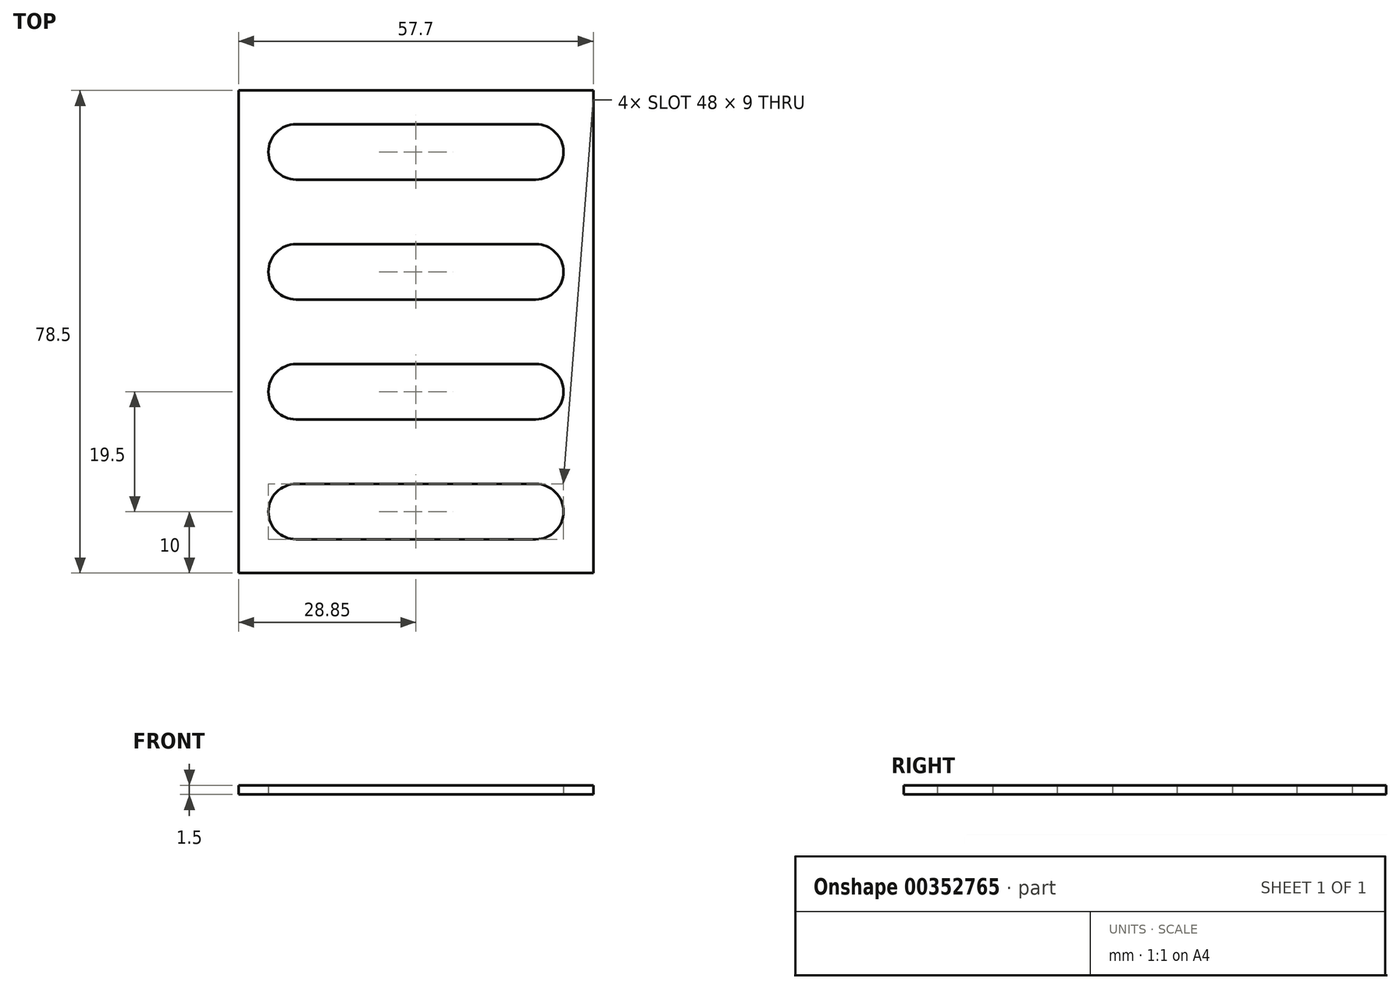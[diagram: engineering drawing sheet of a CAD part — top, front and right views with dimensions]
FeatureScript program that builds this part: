
annotation { "Feature Type Name" : "Feature", "Feature Type Description" : "" }
export const myFeature = defineFeature(function(context is Context, id is Id, definition is map)
    precondition{}
    {
        {
            var Q0;
            Q0=qCreatedBy(makeId("Top.planeOp"),FACE);
            var sketch = newSketch(context, id + "F0", { "sketchPlane" : qUnion([Q0])});
            skLineSegment(sketch, "E0.bottom", {"start": v(28.85, 39.25) * mm, "end": v(-28.85, 39.25) * mm});
            skLineSegment(sketch, "E0.top", {"start": v(28.85, -39.25) * mm, "end": v(-28.85, -39.25) * mm});
            skLineSegment(sketch, "E0.left", {"start": v(28.85, 39.25) * mm, "end": v(28.85, -39.25) * mm});
            skLineSegment(sketch, "E0.right", {"start": v(-28.85, 39.25) * mm, "end": v(-28.85, -39.25) * mm});
            skPoint(sketch, "E0.middle", {"position": v(0, 0) * mm});
            skLineSegment(sketch, "E1", {"start": v(-19.5, 29.25) * mm, "end": v(19.5, 29.25) * mm});
            skPoint(sketch, "E2", {"position": v(0, 29.25) * mm});
            skArc(sketch, "E3.0.startCap", {"start": v(-19.5, 24.75) * mm, "mid": v(-24, 29.25) * mm, "end": v(-19.5, 33.75) * mm});
            skArc(sketch, "E3.0.endCap", {"start": v(19.5, 33.75) * mm, "mid": v(24, 29.25) * mm, "end": v(19.5, 24.75) * mm});
            skLineSegment(sketch, "E3.0.left", {"start": v(-19.5, 33.75) * mm, "end": v(19.5, 33.75) * mm});
            skLineSegment(sketch, "E3.0.right", {"start": v(-19.5, 24.75) * mm, "end": v(19.5, 24.75) * mm});
            skLineSegment(sketch, "E4.0.1.0", {"start": v(-19.5, 5.25) * mm, "end": v(19.5, 5.25) * mm});
            skArc(sketch, "E4.0.1.1", {"start": v(-19.5, 5.25) * mm, "mid": v(-24, 9.75) * mm, "end": v(-19.5, 14.25) * mm});
            skLineSegment(sketch, "E4.0.1.2", {"start": v(-19.5, 14.25) * mm, "end": v(19.5, 14.25) * mm});
            skArc(sketch, "E4.0.1.3", {"start": v(19.5, 14.25) * mm, "mid": v(24, 9.75) * mm, "end": v(19.5, 5.25) * mm});
            skLineSegment(sketch, "E4.0.2.0", {"start": v(-19.5, -14.25) * mm, "end": v(19.5, -14.25) * mm});
            skArc(sketch, "E4.0.2.1", {"start": v(-19.5, -14.25) * mm, "mid": v(-24, -9.75) * mm, "end": v(-19.5, -5.25) * mm});
            skLineSegment(sketch, "E4.0.2.2", {"start": v(-19.5, -5.25) * mm, "end": v(19.5, -5.25) * mm});
            skArc(sketch, "E4.0.2.3", {"start": v(19.5, -5.25) * mm, "mid": v(24, -9.75) * mm, "end": v(19.5, -14.25) * mm});
            skLineSegment(sketch, "E4.0.3.0", {"start": v(-19.5, -33.75) * mm, "end": v(19.5, -33.75) * mm});
            skArc(sketch, "E4.0.3.1", {"start": v(-19.5, -33.75) * mm, "mid": v(-24, -29.25) * mm, "end": v(-19.5, -24.75) * mm});
            skLineSegment(sketch, "E4.0.3.2", {"start": v(-19.5, -24.75) * mm, "end": v(19.5, -24.75) * mm});
            skArc(sketch, "E4.0.3.3", {"start": v(19.5, -24.75) * mm, "mid": v(24, -29.25) * mm, "end": v(19.5, -33.75) * mm});
            skLineSegment(sketch, "E4.direction1", {"start": v(-19.5, 29.25) * mm, "end": v(5.5, 29.25) * mm, "construction": true});
            skLineSegment(sketch, "E4.direction2", {"start": v(-19.5, 29.25) * mm, "end": v(-19.5, 9.75) * mm, "construction": true});
            skSolve(sketch);
        }
        {
            var Q0;
            Q0 = qSketchRegion(id + "F0", true);
            extrude(context, id + "F1", {"entities" : qUnion([Q0]), "depth" : 1.5 * mm});
        }
    });
